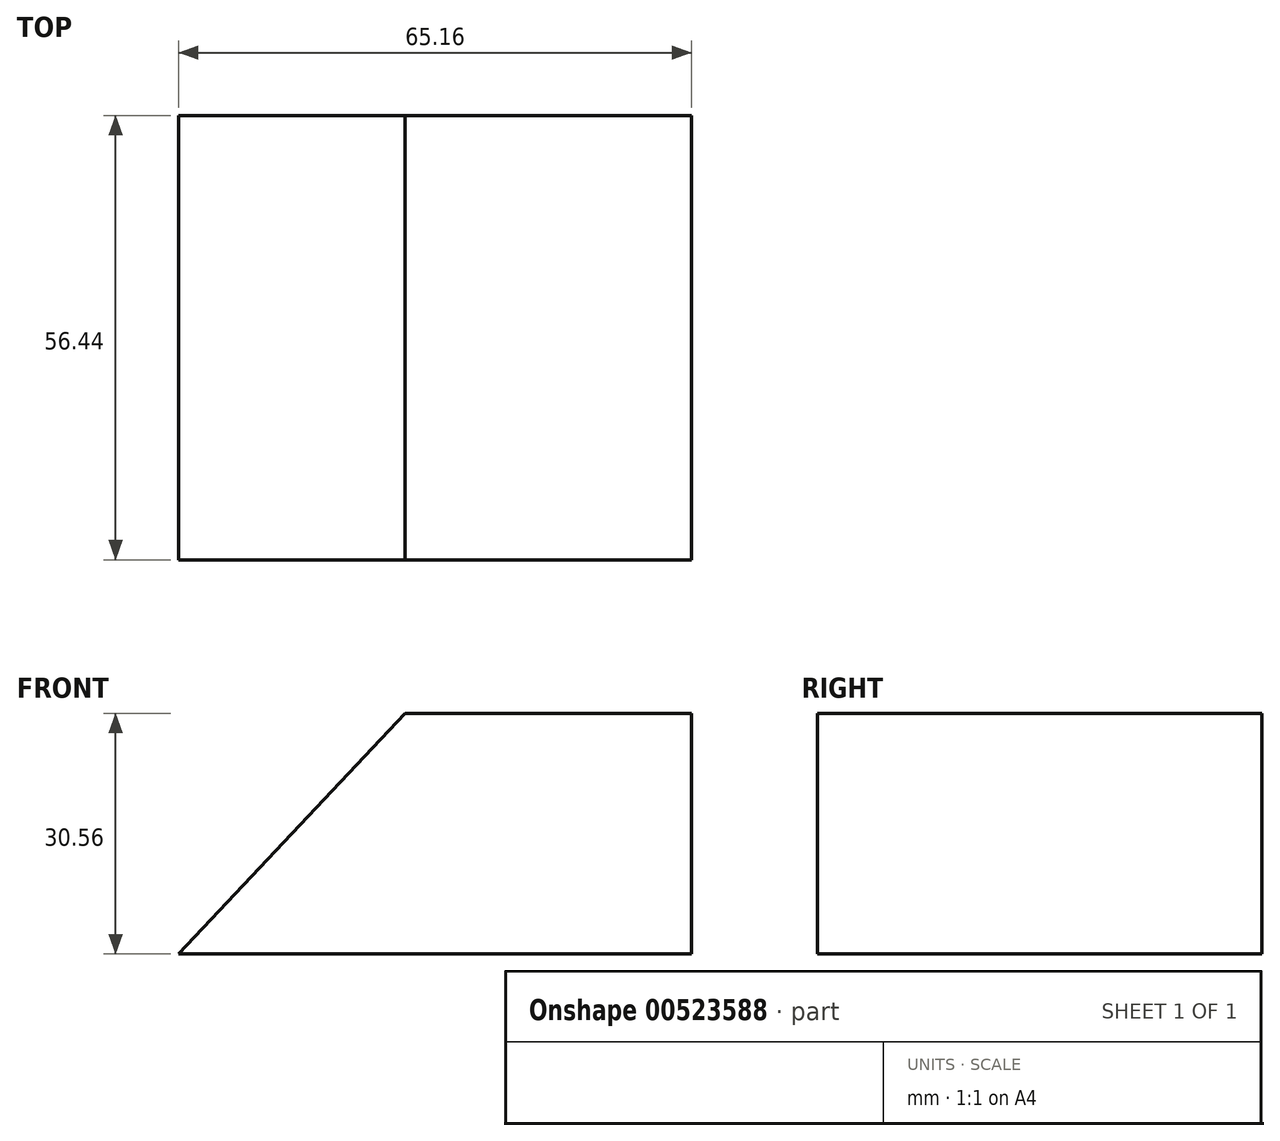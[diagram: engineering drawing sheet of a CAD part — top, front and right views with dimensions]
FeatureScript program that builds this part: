
annotation { "Feature Type Name" : "Feature", "Feature Type Description" : "" }
export const myFeature = defineFeature(function(context is Context, id is Id, definition is map)
    precondition{}
    {
        {
            var Q0;
            Q0=qCreatedBy(makeId("Front.planeOp"),FACE);
            var sketch = newSketch(context, id + "F0", { "sketchPlane" : qUnion([Q0])});
            skLineSegment(sketch, "E0", {"start": v(0, 0) * mm, "end": v(28.79, 30.56) * mm});
            skLineSegment(sketch, "E1", {"start": v(28.79, 30.56) * mm, "end": v(65.16, 30.56) * mm});
            skLineSegment(sketch, "E2", {"start": v(65.16, 30.56) * mm, "end": v(65.16, 0) * mm});
            skLineSegment(sketch, "E3", {"start": v(65.16, 0) * mm, "end": v(0, 0) * mm});
            skSolve(sketch);
        }
        {
            var Q0;
            Q0 = qSketchRegion(id + "F0", true);
            extrude(context, id + "F1", {"entities" : qUnion([Q0]), "depth" : 56.44 * mm, "offsetDistance" : 25.4 * mm});
        }
    });
